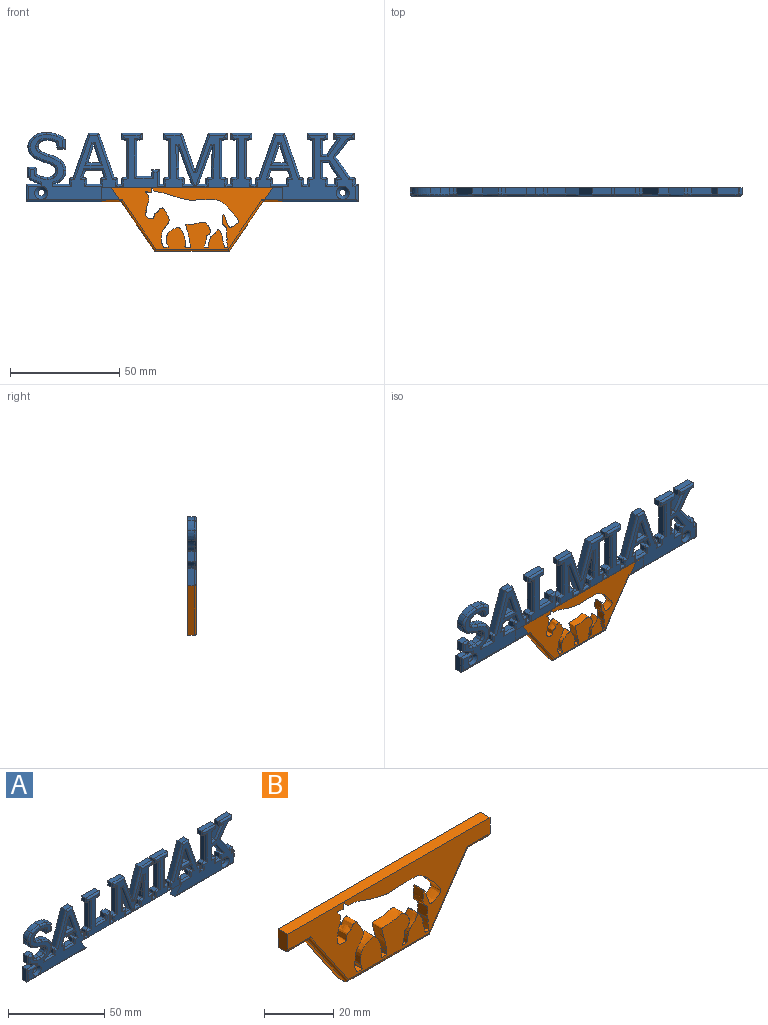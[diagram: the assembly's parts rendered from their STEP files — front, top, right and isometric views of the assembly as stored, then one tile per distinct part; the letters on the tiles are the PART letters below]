
ASSEMBLY  parts=2 mates=1
PART A: 335 faces, bbox 152.3x4.3x31.9 mm
  f0: plane 150x29.63mm, normal (0,-1,0), area 1480.1mm2, adj f3,f166,f167,f168,f169,f170,f171,f172
  f1: plane 152x31.63mm, normal (0,1,0), area 2472.2mm2, adj f2,f4,f5,f6,f7,f8,f9,f10
  f2: plane 43.45x3mm, normal (0,0,-1), area 130.3mm2, adj f1,f3,f47,f331
  f3: cylinder r=1mm len=43.45mm, axis (-1,0,0), area 66.9mm2, adj f0,f2,f276,f331
  f4: extruded ~3x1.6mm, area 5mm2, adj f1,f35,f165,f270
  f5: plane 3x2.77mm, normal (-1,0,0), area 8.3mm2, adj f1,f17,f160,f190
  f6: plane 6.49x3mm, normal (1,0,0), area 19.5mm2, adj f1,f7,f159,f166
  f7: plane 3.57x3mm, normal (0,0,1), area 10.7mm2, adj f1,f6,f8,f168
  f8: plane 3x2.93mm, normal (-1,0,0.08), area 8.8mm2, adj f1,f7,f9,f170
  f9: plane 6.58x3mm, normal (0,0,1), area 19.7mm2, adj f1,f8,f10,f172
  f10: plane 16.42x3mm, normal (1,0,0), area 49.3mm2, adj f1,f9,f11,f174
  f11: plane 3x2.49mm, normal (0.19,0,-0.98), area 7.6mm2, adj f1,f10,f12,f176
  f12: plane 3x2.82mm, normal (1,0,0), area 8.5mm2, adj f1,f11,f13,f178
  f13: plane 9.65x3mm, normal (0,0,1), area 28.9mm2, adj f1,f12,f14,f180
  f14: plane 3x2.82mm, normal (-1,0,0), area 8.5mm2, adj f1,f13,f15,f182
  f15: plane 3x2.48mm, normal (-0.19,0,-0.98), area 7.6mm2, adj f1,f14,f16,f184
  f16: plane 16.72x3mm, normal (-1,0,0), area 50.2mm2, adj f1,f15,f17,f186
  f17: plane 3x2.48mm, normal (-0.19,0,0.98), area 7.6mm2, adj f1,f5,f16,f188
  f18: plane 3.5x3mm, normal (0,0,-1), area 10.5mm2, adj f1,f19,f46,f234
  f19: plane 4.77x3mm, normal (1,0,0), area 14.3mm2, adj f1,f18,f20,f236
  f20: extruded ~3.71x3mm, area 13mm2, adj f1,f19,f21,f238
  f21: extruded ~4.9x3mm, area 15mm2, adj f1,f20,f22,f240
  f22: extruded ~6.03x3mm, area 19.3mm2, adj f1,f21,f23,f242
  f23: extruded ~4.63x3mm, area 16.3mm2, adj f1,f22,f24,f244
  f24: extruded ~4.51x3mm, area 15.5mm2, adj f1,f23,f25,f246
  f25: extruded ~6.28x3mm, area 20.8mm2, adj f1,f24,f26,f248
  f26: extruded ~3.33x3mm, area 11.1mm2, adj f1,f25,f27,f250
  f27: extruded ~3x2.16mm, area 7.3mm2, adj f1,f26,f28,f252
  f28: extruded ~3x2.1mm, area 7.2mm2, adj f1,f27,f29,f254
  f29: extruded ~3x2.92mm, area 9.2mm2, adj f1,f28,f30,f256
  f30: extruded ~3x2.7mm, area 8.2mm2, adj f1,f29,f31,f258
  f31: extruded ~3x1.91mm, area 6.4mm2, adj f1,f30,f32,f260
  f32: plane 3.31x3mm, normal (0.99,0,0.15), area 10.1mm2, adj f1,f31,f33,f262
  f33: plane 3.62x3mm, normal (0,0,1), area 10.8mm2, adj f1,f32,f34,f264
  f34: plane 4.87x3mm, normal (-1,0,0), area 14.6mm2, adj f1,f33,f35,f266
  f35: extruded ~3.72x3mm, area 13.4mm2, adj f1,f4,f34,f268
  f36: extruded ~3x2.9mm, area 9.6mm2, adj f1,f37,f163,f212
  f37: extruded ~4.72x3mm, area 16.5mm2, adj f1,f36,f38,f214
  f38: extruded ~4.62x3mm, area 15.6mm2, adj f1,f37,f39,f216
  f39: extruded ~5.85x3mm, area 19.7mm2, adj f1,f38,f40,f218
  f40: extruded ~3.79x3mm, area 12.4mm2, adj f1,f39,f41,f220
  f41: extruded ~3x1.94mm, area 7mm2, adj f1,f40,f42,f222
  f42: extruded ~3x2.09mm, area 7.3mm2, adj f1,f41,f43,f224
  f43: extruded ~3x2.97mm, area 9.4mm2, adj f1,f42,f44,f226
  f44: extruded ~3x2.48mm, area 7.5mm2, adj f1,f43,f45,f228
  f45: extruded ~3x1.78mm, area 5.7mm2, adj f1,f44,f46,f230
  f46: plane 3.2x3mm, normal (-0.98,0,-0.19), area 9.8mm2, adj f1,f18,f45,f232
  f47: plane 8.03x3mm, normal (-1,0,0), area 24.1mm2, adj f1,f2,f164,f276
  f48: plane 43.45x3mm, normal (0,0,-1), area 130.3mm2, adj f1,f49,f278,f332
  f49: plane 8.03x3mm, normal (1,0,0), area 24.1mm2, adj f1,f48,f151,f280
  f50: plane 5.35x3mm, normal (0,0,1), area 16mm2, adj f1,f51,f67,f324
  f51: plane 8.21x3mm, normal (0.95,0,-0.3), area 25.9mm2, adj f1,f50,f52,f326
  f52: plane 3x0.09mm, normal (0,0,-1), area 0.3mm2, adj f1,f51,f67,f327
  f53: plane 3x1.66mm, normal (-0.14,0,0.99), area 5mm2, adj f1,f54,f66,f204
  f54: plane 3x2.77mm, normal (-1,0,0), area 8.3mm2, adj f1,f53,f162,f206
  f55: plane 3x2.77mm, normal (1,0,0), area 8.3mm2, adj f1,f56,f161,f317
  f56: plane 3x1.61mm, normal (0.18,0,0.98), area 4.9mm2, adj f1,f55,f57,f315
  f57: plane 3.2x3mm, normal (0.95,0,-0.3), area 10.1mm2, adj f1,f56,f58,f313
  f58: plane 7.55x3mm, normal (0,0,-1), area 22.7mm2, adj f1,f57,f59,f312
  f59: plane 3.2x3mm, normal (-0.95,0,-0.3), area 10.1mm2, adj f1,f58,f60,f314
  f60: plane 3x1.62mm, normal (-0.17,0,0.98), area 4.9mm2, adj f1,f59,f61,f316
  f61: plane 3x2.77mm, normal (-1,0,0), area 8.3mm2, adj f1,f60,f161,f318
  f62: plane 3x2.77mm, normal (1,0,0), area 8.3mm2, adj f1,f63,f160,f194
  f63: plane 3x1.66mm, normal (0.14,0,0.99), area 5mm2, adj f1,f62,f64,f196
  f64: plane 20.26x7.04mm, normal (0.94,0,0.33), area 64.3mm2, adj f1,f63,f65,f198
  f65: plane 4.78x3mm, normal (0,0,1), area 14.4mm2, adj f1,f64,f66,f200
  f66: plane 20.26x7.09mm, normal (-0.94,0,0.33), area 64.4mm2, adj f1,f53,f65,f202
  f67: plane 8.21x3mm, normal (-0.95,0,-0.3), area 25.9mm2, adj f1,f50,f52,f325
  f68: plane 3x0.1mm, normal (-0.16,0,-0.99), area 0.3mm2, adj f1,f69,f94,f300
  f69: plane 10.29x3mm, normal (-1,0,0.04), area 30.9mm2, adj f1,f68,f70,f298
  f70: plane 3.66x3mm, normal (-1,0,0), area 11mm2, adj f1,f69,f71,f299
  f71: plane 3x2.48mm, normal (-0.19,0,0.98), area 7.6mm2, adj f1,f70,f72,f301
  f72: plane 3x2.77mm, normal (-1,0,0), area 8.3mm2, adj f1,f71,f157,f303
  f73: plane 3x2.77mm, normal (1,0,0), area 8.3mm2, adj f1,f74,f156,f197
  f74: plane 3x2.49mm, normal (0.19,0,0.98), area 7.6mm2, adj f1,f73,f75,f195
  f75: plane 16.72x3mm, normal (1,0,0), area 50.2mm2, adj f1,f74,f76,f193
  f76: plane 3x2.49mm, normal (0.19,0,-0.98), area 7.6mm2, adj f1,f75,f77,f191
  f77: plane 3x2.82mm, normal (1,0,0), area 8.5mm2, adj f1,f76,f78,f189
  f78: plane 8.61x3mm, normal (0,0,1), area 25.8mm2, adj f1,f77,f79,f187
  f79: plane 17.17x5.99mm, normal (-0.94,0,0.33), area 54.6mm2, adj f1,f78,f80,f185
  f80: plane 3x0.1mm, normal (0,0,1), area 0.3mm2, adj f1,f79,f81,f183
  f81: plane 17.17x5.94mm, normal (0.95,0,0.33), area 54.5mm2, adj f1,f80,f82,f181
  f82: plane 8.58x3mm, normal (0,0,1), area 25.7mm2, adj f1,f81,f83,f179
  f83: plane 3x2.82mm, normal (-1,0,0), area 8.5mm2, adj f1,f82,f84,f177
  f84: plane 3x2.48mm, normal (-0.19,0,-0.98), area 7.6mm2, adj f1,f83,f85,f175
  f85: plane 16.72x3mm, normal (-1,0,0), area 50.2mm2, adj f1,f84,f86,f173
  f86: plane 3x2.48mm, normal (-0.19,0,0.98), area 7.6mm2, adj f1,f85,f87,f171
  f87: plane 3x2.77mm, normal (-1,0,0), area 8.3mm2, adj f1,f86,f159,f169
  f88: plane 3x2.77mm, normal (1,0,0), area 8.3mm2, adj f1,f89,f158,f309
  f89: plane 3x2.49mm, normal (0.19,0,0.98), area 7.6mm2, adj f1,f88,f90,f307
  f90: plane 3.66x3mm, normal (1,0,0), area 11mm2, adj f1,f89,f91,f305
  f91: plane 10.23x3mm, normal (1,0,0.04), area 30.7mm2, adj f1,f90,f92,f306
  f92: plane 3x0.1mm, normal (0.16,0,-0.99), area 0.3mm2, adj f1,f91,f93,f308
  f93: plane 17.16x6.2mm, normal (-0.94,0,-0.34), area 54.7mm2, adj f1,f92,f158,f310
  f94: plane 17.23x6.23mm, normal (0.94,0,-0.34), area 55mm2, adj f1,f68,f157,f302
  f95: plane 3x2.82mm, normal (-1,0,0), area 8.5mm2, adj f1,f96,f105,f209
  f96: plane 3x2.49mm, normal (-0.19,0,-0.98), area 7.6mm2, adj f1,f95,f97,f207
  f97: plane 16.72x3mm, normal (-1,0,0), area 50.2mm2, adj f1,f96,f98,f205
  f98: plane 3x2.49mm, normal (-0.19,0,0.98), area 7.6mm2, adj f1,f97,f99,f203
  f99: plane 3x2.77mm, normal (-1,0,0), area 8.3mm2, adj f1,f98,f156,f201
  f100: plane 3x2.77mm, normal (1,0,0), area 8.3mm2, adj f1,f101,f155,f221
  f101: plane 3x2.49mm, normal (0.19,0,0.98), area 7.6mm2, adj f1,f100,f102,f219
  f102: plane 16.72x3mm, normal (1,0,0), area 50.2mm2, adj f1,f101,f103,f217
  f103: plane 3x2.49mm, normal (0.19,0,-0.98), area 7.6mm2, adj f1,f102,f104,f215
  f104: plane 3x2.82mm, normal (1,0,0), area 8.5mm2, adj f1,f103,f105,f213
  f105: plane 9.65x3mm, normal (0,0,1), area 28.9mm2, adj f1,f95,f104,f211
  f106: plane 5.35x3mm, normal (0,0,1), area 16mm2, adj f1,f107,f123,f320
  f107: plane 8.21x3mm, normal (0.95,0,-0.3), area 25.9mm2, adj f1,f106,f108,f322
  f108: plane 3x0.09mm, normal (0,0,-1), area 0.3mm2, adj f1,f107,f123,f323
  f109: plane 3x1.66mm, normal (-0.14,0,0.99), area 5mm2, adj f1,f110,f122,f227
  f110: plane 3x2.77mm, normal (-1,0,0), area 8.3mm2, adj f1,f109,f155,f225
  f111: plane 3x2.77mm, normal (1,0,0), area 8.3mm2, adj f1,f112,f154,f295
  f112: plane 3x1.61mm, normal (0.18,0,0.98), area 4.9mm2, adj f1,f111,f113,f293
  f113: plane 3.2x3mm, normal (0.95,0,-0.3), area 10.1mm2, adj f1,f112,f114,f291
  f114: plane 7.55x3mm, normal (0,0,-1), area 22.7mm2, adj f1,f113,f115,f290
  f115: plane 3.2x3mm, normal (-0.95,0,-0.3), area 10.1mm2, adj f1,f114,f116,f292
  f116: plane 3x1.62mm, normal (-0.17,0,0.98), area 4.9mm2, adj f1,f115,f117,f294
  f117: plane 3x2.77mm, normal (-1,0,0), area 8.3mm2, adj f1,f116,f154,f296
  f118: plane 3x2.77mm, normal (1,0,0), area 8.3mm2, adj f1,f119,f153,f237
  f119: plane 3x1.66mm, normal (0.14,0,0.99), area 5mm2, adj f1,f118,f120,f235
  f120: plane 20.26x7.04mm, normal (0.94,0,0.33), area 64.3mm2, adj f1,f119,f121,f233
  f121: plane 4.78x3mm, normal (0,0,1), area 14.4mm2, adj f1,f120,f122,f231
  f122: plane 20.26x7.09mm, normal (-0.94,0,0.33), area 64.4mm2, adj f1,f109,f121,f229
  f123: plane 8.21x3mm, normal (-0.95,0,-0.3), area 25.9mm2, adj f1,f106,f108,f321
  f124: plane 3x2.48mm, normal (-0.19,0,0.98), area 7.6mm2, adj f1,f125,f150,f243
  f125: plane 3x2.77mm, normal (-1,0,0), area 8.3mm2, adj f1,f124,f153,f241
  f126: plane 3x2.77mm, normal (1,0,0), area 8.3mm2, adj f1,f127,f152,f287
  f127: plane 3x2.37mm, normal (0.2,0,0.98), area 7.2mm2, adj f1,f126,f128,f285
  f128: plane 6.45x3mm, normal (1,0,0), area 19.3mm2, adj f1,f127,f129,f283
  f129: plane 3x2.61mm, normal (0,0,-1), area 7.8mm2, adj f1,f128,f130,f282
  f130: plane 6.74x4.48mm, normal (-0.83,0,-0.55), area 24.3mm2, adj f1,f129,f131,f284
  f131: plane 3x1.44mm, normal (-0.13,0,0.99), area 4.4mm2, adj f1,f130,f132,f286
  f132: plane 3x2.77mm, normal (-1,0,0), area 8.3mm2, adj f1,f131,f152,f288
  f133: plane 3x2.77mm, normal (1,0,0), area 8.3mm2, adj f1,f134,f151,f279
  f134: plane 3x2.34mm, normal (0.17,0,0.99), area 7.1mm2, adj f1,f133,f135,f277
  f135: plane 9.2x6.43mm, normal (0.82,0,0.57), area 33.7mm2, adj f1,f134,f136,f275
  f136: plane 7.65x5.73mm, normal (0.8,0,-0.6), area 28.7mm2, adj f1,f135,f137,f273
  f137: plane 3x2.53mm, normal (0.17,0,-0.99), area 7.7mm2, adj f1,f136,f138,f271
  f138: plane 3x2.82mm, normal (1,0,0), area 8.5mm2, adj f1,f137,f139,f269
  f139: plane 9.23x3mm, normal (0,0,1), area 27.7mm2, adj f1,f138,f140,f267
  f140: plane 3x2.82mm, normal (-1,0,0), area 8.5mm2, adj f1,f139,f141,f265
  f141: plane 3x1.38mm, normal (-0.14,0,-0.99), area 4.2mm2, adj f1,f140,f142,f263
  f142: plane 6.51x4.48mm, normal (-0.82,0,0.57), area 23.7mm2, adj f1,f141,f143,f261
  f143: plane 3x2.03mm, normal (0,0,1), area 6.1mm2, adj f1,f142,f144,f259
  f144: plane 6.22x3mm, normal (1,0,0), area 18.7mm2, adj f1,f143,f145,f257
  f145: plane 3x2.37mm, normal (0.2,0,-0.98), area 7.2mm2, adj f1,f144,f146,f255
  f146: plane 3x2.82mm, normal (1,0,0), area 8.5mm2, adj f1,f145,f147,f253
  f147: plane 9.52x3mm, normal (0,0,1), area 28.6mm2, adj f1,f146,f148,f251
  f148: plane 3x2.82mm, normal (-1,0,0), area 8.5mm2, adj f1,f147,f149,f249
  f149: plane 3x2.48mm, normal (-0.19,0,-0.98), area 7.6mm2, adj f1,f148,f150,f247
  f150: plane 16.72x3mm, normal (-1,0,0), area 50.2mm2, adj f1,f124,f149,f245
  f151: plane 3x1.31mm, normal (0,0,1), area 3.9mm2, adj f1,f49,f133,f281
  f152: plane 3.28x3mm, normal (0,0,1), area 9.8mm2, adj f1,f126,f132,f289
  f153: plane 3x1.54mm, normal (0,0,1), area 4.6mm2, adj f1,f118,f125,f239
  f154: plane 6.37x3mm, normal (0,0,1), area 19.1mm2, adj f1,f111,f117,f297
  f155: plane 3x1.54mm, normal (0,0,1), area 4.6mm2, adj f1,f100,f110,f223
  f156: plane 3x1.65mm, normal (0,0,1), area 4.9mm2, adj f1,f73,f99,f199
  f157: plane 3.4x3mm, normal (0,0,1), area 10.2mm2, adj f1,f72,f94,f304
  f158: plane 3.35x3mm, normal (0,0,1), area 10.1mm2, adj f1,f88,f93,f311
  f159: plane 3x1.68mm, normal (0,0,1), area 5mm2, adj f1,f6,f87,f167
  f160: plane 3x1.54mm, normal (0,0,1), area 4.6mm2, adj f1,f5,f62,f192
  f161: plane 6.37x3mm, normal (0,0,1), area 19.1mm2, adj f1,f55,f61,f319
  f162: plane 6.87x3mm, normal (0,0,1), area 20.6mm2, adj f1,f54,f163,f208
  f163: plane 3x0.02mm, normal (1,0,0), area 0.1mm2, adj f1,f36,f162,f210
  f164: plane 6.22x3mm, normal (0,0,1), area 18.7mm2, adj f1,f47,f165,f274
  f165: plane 3x0.01mm, normal (-1,0,0), area 0mm2, adj f1,f4,f164,f272
  f166: cylinder r=1mm len=7.49mm, axis (0,0,-1), area 10.2mm2, adj f0,f6,f167,f168
  f167: cylinder r=1mm len=3.68mm, axis (1,0,0), area 4.2mm2, adj f0,f159,f166,f169
  f168: cylinder r=1mm len=3.57mm, axis (1,0,0), area 4.1mm2, adj f0,f7,f166,f170
  f169: cylinder r=1mm len=3.77mm, axis (0,0,1), area 4.5mm2, adj f0,f87,f167,f171
  f170: cylinder r=1mm len=3.93mm, axis (0.08,0,1), area 4.6mm2, adj f0,f8,f168,f172
  f171: cylinder r=1mm len=3.48mm, axis (0.98,0,0.19), area 4mm2, adj f0,f86,f169,f173
  f172: cylinder r=1mm len=8.5mm, axis (1,0,0), area 11.8mm2, adj f0,f9,f170,f174
  f173: cylinder r=1mm len=18.37mm, axis (0,0,1), area 27.6mm2, adj f0,f85,f171,f175
  f174: cylinder r=1mm len=18.25mm, axis (0,0,-1), area 27.2mm2, adj f0,f10,f172,f176
  f175: cylinder r=1mm len=3.48mm, axis (-0.98,0,0.19), area 4mm2, adj f0,f84,f173,f177
  f176: cylinder r=1mm len=3.49mm, axis (-0.98,0,-0.19), area 4mm2, adj f0,f11,f174,f178
  f177: cylinder r=1mm len=2.82mm, axis (0,0,1), area 3mm2, adj f0,f83,f175,f179
  f178: cylinder r=1mm len=2.82mm, axis (0,0,-1), area 3mm2, adj f0,f12,f176,f180
  f179: cylinder r=1mm len=8.58mm, axis (1,0,0), area 12.1mm2, adj f0,f82,f177,f181
  f180: cylinder r=1mm len=9.65mm, axis (1,0,0), area 13.6mm2, adj f0,f13,f178,f182
  f181: cylinder r=1mm len=18.17mm, axis (0.33,0,-0.95), area 28.5mm2, adj f0,f81,f179,f183
  f182: cylinder r=1mm len=2.82mm, axis (0,0,1), area 3mm2, adj f0,f14,f180,f184
  f183: cylinder r=1mm len=1.52mm, axis (1,0,0), area 1mm2, adj f0,f80,f181,f185
  f184: cylinder r=1mm len=3.48mm, axis (-0.98,0,0.19), area 4mm2, adj f0,f15,f182,f186
  f185: cylinder r=1mm len=18.17mm, axis (0.33,0,0.94), area 28.6mm2, adj f0,f79,f183,f187
  f186: cylinder r=1mm len=18.37mm, axis (0,0,1), area 27.6mm2, adj f0,f16,f184,f188
  f187: cylinder r=1mm len=8.61mm, axis (1,0,0), area 12.2mm2, adj f0,f78,f185,f189
  f188: cylinder r=1mm len=3.48mm, axis (0.98,0,0.19), area 4mm2, adj f0,f17,f186,f190
  f189: cylinder r=1mm len=2.82mm, axis (0,0,-1), area 3mm2, adj f0,f77,f187,f191
  f190: cylinder r=1mm len=3.77mm, axis (0,0,1), area 4.5mm2, adj f0,f5,f188,f192
  f191: cylinder r=1mm len=3.49mm, axis (-0.98,0,-0.19), area 4mm2, adj f0,f76,f189,f193
  f192: cylinder r=1mm len=3.54mm, axis (1,0,0), area 4mm2, adj f0,f160,f190,f194
  f193: cylinder r=1mm len=18.37mm, axis (0,0,-1), area 27.6mm2, adj f0,f75,f191,f195
  f194: cylinder r=1mm len=3.77mm, axis (0,0,-1), area 4.5mm2, adj f0,f62,f192,f196
  f195: cylinder r=1mm len=3.49mm, axis (0.98,0,-0.19), area 4mm2, adj f0,f74,f193,f197
  f196: cylinder r=1mm len=2.41mm, axis (0.99,0,-0.14), area 2.4mm2, adj f0,f63,f194,f198
  f197: cylinder r=1mm len=3.77mm, axis (0,0,-1), area 4.5mm2, adj f0,f73,f195,f199
  f198: cylinder r=1mm len=21.16mm, axis (0.33,0,-0.94), area 33.6mm2, adj f0,f64,f196,f200
  f199: cylinder r=1mm len=3.65mm, axis (1,0,0), area 4.2mm2, adj f0,f156,f197,f201
  f200: cylinder r=1mm len=4.78mm, axis (1,0,0), area 6.4mm2, adj f0,f65,f198,f202
  f201: cylinder r=1mm len=3.77mm, axis (0,0,1), area 4.5mm2, adj f0,f99,f199,f203
  f202: cylinder r=1mm len=21.16mm, axis (0.33,0,0.94), area 33.6mm2, adj f0,f66,f200,f204
  f203: cylinder r=1mm len=3.49mm, axis (0.98,0,0.19), area 4mm2, adj f0,f98,f201,f205
  f204: cylinder r=1mm len=2.41mm, axis (0.99,0,0.14), area 2.4mm2, adj f0,f53,f202,f206
  f205: cylinder r=1mm len=18.37mm, axis (0,0,1), area 27.6mm2, adj f0,f97,f203,f207
  f206: cylinder r=1mm len=3.77mm, axis (0,0,1), area 4.5mm2, adj f0,f54,f204,f208
  f207: cylinder r=1mm len=3.49mm, axis (-0.98,0,0.19), area 4mm2, adj f0,f96,f205,f209
  f208: cylinder r=1mm len=8.87mm, axis (1,0,0), area 12.4mm2, adj f0,f162,f206,f210
  f209: cylinder r=1mm len=2.82mm, axis (0,0,1), area 3mm2, adj f0,f95,f207,f211
  f210: cylinder r=1mm len=1.83mm, axis (0,0,1), area 1.1mm2, adj f0,f163,f208,f212
  f211: cylinder r=1mm len=9.65mm, axis (1,0,0), area 13.6mm2, adj f0,f105,f209,f213
  f212: bspline ~5.54x3.25mm, area 5.5mm2, adj f0,f36,f210,f214
  f213: cylinder r=1mm len=2.82mm, axis (0,0,-1), area 3mm2, adj f0,f104,f211,f215
  f214: bspline ~5.93x4.09mm, area 8.1mm2, adj f0,f37,f212,f216
  f215: cylinder r=1mm len=3.49mm, axis (-0.98,0,-0.19), area 4mm2, adj f0,f103,f213,f217
  f216: bspline ~7.17x3.8mm, area 7.7mm2, adj f0,f38,f214,f218
  f217: cylinder r=1mm len=18.37mm, axis (0,0,-1), area 27.6mm2, adj f0,f102,f215,f219
  f218: bspline ~8.49x4.64mm, area 10mm2, adj f0,f39,f216,f220
  f219: cylinder r=1mm len=3.49mm, axis (0.98,0,-0.19), area 4mm2, adj f0,f101,f217,f221
  f220: bspline ~5.52x2.97mm, area 6.7mm2, adj f0,f40,f218,f222
  f221: cylinder r=1mm len=3.77mm, axis (0,0,-1), area 4.5mm2, adj f0,f100,f219,f223
  f222: bspline ~3.7x2.58mm, area 4.2mm2, adj f0,f41,f220,f224
  f223: cylinder r=1mm len=3.54mm, axis (1,0,0), area 4mm2, adj f0,f155,f221,f225
  f224: bspline ~3.89x2.54mm, area 4.3mm2, adj f0,f42,f222,f226
  f225: cylinder r=1mm len=3.77mm, axis (0,0,1), area 4.5mm2, adj f0,f110,f223,f227
  f226: bspline ~4.93x1.89mm, area 5.3mm2, adj f0,f43,f224,f228
  f227: cylinder r=1mm len=2.41mm, axis (0.99,0,0.14), area 2.4mm2, adj f0,f109,f225,f229
  f228: bspline ~3.3x1.4mm, area 4.1mm2, adj f0,f44,f226,f230
  f229: cylinder r=1mm len=21.16mm, axis (0.33,0,0.94), area 33.6mm2, adj f0,f122,f227,f231
  f230: bspline ~3.75x2.33mm, area 3.5mm2, adj f0,f45,f228,f232
  f231: cylinder r=1mm len=4.78mm, axis (1,0,0), area 6.4mm2, adj f0,f121,f229,f233
  f232: cylinder r=1mm len=3.82mm, axis (-0.19,0,0.98), area 4.8mm2, adj f0,f46,f230,f234
  f233: cylinder r=1mm len=21.16mm, axis (0.33,0,-0.94), area 33.6mm2, adj f0,f120,f231,f235
  f234: cylinder r=1mm len=3.5mm, axis (-1,0,0), area 4.1mm2, adj f0,f18,f232,f236
  f235: cylinder r=1mm len=2.41mm, axis (0.99,0,-0.14), area 2.4mm2, adj f0,f119,f233,f237
  f236: cylinder r=1mm len=4.77mm, axis (0,0,-1), area 6.3mm2, adj f0,f19,f234,f238
  f237: cylinder r=1mm len=3.77mm, axis (0,0,-1), area 4.5mm2, adj f0,f118,f235,f239
  f238: bspline ~5.31x3.52mm, area 6.2mm2, adj f0,f20,f236,f240
  f239: cylinder r=1mm len=3.54mm, axis (1,0,0), area 4mm2, adj f0,f153,f237,f241
  f240: bspline ~6.2x2.17mm, area 7.6mm2, adj f0,f21,f238,f242
  f241: cylinder r=1mm len=3.77mm, axis (0,0,1), area 4.5mm2, adj f0,f125,f239,f243
  f242: bspline ~7.58x3.65mm, area 9.7mm2, adj f0,f22,f240,f244
  f243: cylinder r=1mm len=3.48mm, axis (0.98,0,0.19), area 4mm2, adj f0,f124,f241,f245
  f244: bspline ~6.88x4.13mm, area 8mm2, adj f0,f23,f242,f246
  f245: cylinder r=1mm len=18.37mm, axis (0,0,1), area 27.6mm2, adj f0,f150,f243,f247
  f246: bspline ~6.71x3.82mm, area 7.6mm2, adj f0,f24,f244,f248
  f247: cylinder r=1mm len=3.48mm, axis (-0.98,0,0.19), area 4mm2, adj f0,f149,f245,f249
  f248: bspline ~9.03x4.73mm, area 10.7mm2, adj f0,f25,f246,f250
  f249: cylinder r=1mm len=2.82mm, axis (0,0,1), area 3mm2, adj f0,f148,f247,f251
  f250: bspline ~5.31x3.13mm, area 6mm2, adj f0,f26,f248,f252
  f251: cylinder r=1mm len=9.52mm, axis (1,0,0), area 13.4mm2, adj f0,f147,f249,f253
  f252: bspline ~3.94x2.42mm, area 4.3mm2, adj f0,f27,f250,f254
  f253: cylinder r=1mm len=2.82mm, axis (0,0,-1), area 3mm2, adj f0,f146,f251,f255
  f254: bspline ~3.89x2.49mm, area 4.3mm2, adj f0,f28,f252,f256
  f255: cylinder r=1mm len=3.37mm, axis (-0.98,0,-0.2), area 3.8mm2, adj f0,f145,f253,f257
  f256: bspline ~5.2x2.15mm, area 5.2mm2, adj f0,f29,f254,f258
  f257: cylinder r=1mm len=8.04mm, axis (0,0,-1), area 11.2mm2, adj f0,f144,f255,f259
  f258: bspline ~4.08x1.54mm, area 4.5mm2, adj f0,f30,f256,f260
  f259: cylinder r=1mm len=3.56mm, axis (1,0,0), area 4.4mm2, adj f0,f143,f257,f261
  f260: bspline ~3.87x2.69mm, area 3.9mm2, adj f0,f31,f258,f262
  f261: cylinder r=1mm len=8.85mm, axis (0.57,0,0.82), area 14.1mm2, adj f0,f142,f259,f263
  f262: cylinder r=1mm len=3.84mm, axis (0.15,0,-0.99), area 4.9mm2, adj f0,f32,f260,f264
  f263: cylinder r=1mm len=3.12mm, axis (-0.99,0,0.14), area 2.8mm2, adj f0,f141,f261,f265
  f264: cylinder r=1mm len=3.62mm, axis (1,0,0), area 4.2mm2, adj f0,f33,f262,f266
  f265: cylinder r=1mm len=2.82mm, axis (0,0,1), area 3mm2, adj f0,f140,f263,f267
  f266: cylinder r=1mm len=4.87mm, axis (0,0,1), area 6.5mm2, adj f0,f34,f264,f268
  f267: cylinder r=1mm len=9.23mm, axis (1,0,0), area 12.9mm2, adj f0,f139,f265,f269
  f268: bspline ~4.54x3.47mm, area 6.5mm2, adj f0,f35,f266,f270
  f269: cylinder r=1mm len=2.82mm, axis (0,0,-1), area 3mm2, adj f0,f138,f267,f271
  f270: bspline ~4.41x2.16mm, area 3.2mm2, adj f0,f4,f268,f272
  f271: cylinder r=1mm len=3.09mm, axis (-0.99,0,-0.17), area 3.7mm2, adj f0,f137,f269,f273
  f272: cylinder r=1mm len=1.83mm, axis (0,0,-1), area 1.1mm2, adj f0,f165,f270,f274
  f273: cylinder r=1mm len=9.15mm, axis (-0.6,0,-0.8), area 15.9mm2, adj f0,f136,f271,f275
  f274: cylinder r=1mm len=7.22mm, axis (1,0,0), area 9.8mm2, adj f0,f164,f272,f276
  f275: cylinder r=1mm len=10.71mm, axis (0.57,0,-0.82), area 18.5mm2, adj f0,f135,f273,f277
  f276: cylinder r=1mm len=8.03mm, axis (0,0,1), area 11mm2, adj f0,f3,f47,f274
  f277: cylinder r=1mm len=2.92mm, axis (0.99,0,-0.17), area 3.4mm2, adj f0,f134,f275,f279
  f278: cylinder r=1mm len=43.45mm, axis (-1,0,0), area 66.9mm2, adj f0,f48,f280,f332
  f279: cylinder r=1mm len=3.77mm, axis (0,0,-1), area 4.5mm2, adj f0,f133,f277,f281
  f280: cylinder r=1mm len=8.03mm, axis (0,0,-1), area 11mm2, adj f0,f49,f278,f281
  f281: cylinder r=1mm len=2.31mm, axis (1,0,0), area 2.1mm2, adj f0,f151,f279,f280
  f282: cylinder r=1mm len=4.14mm, axis (-1,0,0), area 5.3mm2, adj f0,f129,f283,f284
  f283: cylinder r=1mm len=8.27mm, axis (0,0,-1), area 11.6mm2, adj f0,f128,f282,f285
  f284: cylinder r=1mm len=9.08mm, axis (-0.55,0,0.83), area 14.4mm2, adj f0,f130,f282,f286
  f285: cylinder r=1mm len=3.37mm, axis (0.98,0,-0.2), area 3.8mm2, adj f0,f127,f283,f287
  f286: cylinder r=1mm len=3.16mm, axis (0.99,0,0.13), area 2.9mm2, adj f0,f131,f284,f288
  f287: cylinder r=1mm len=3.77mm, axis (0,0,-1), area 4.5mm2, adj f0,f126,f285,f289
  f288: cylinder r=1mm len=3.77mm, axis (0,0,1), area 4.5mm2, adj f0,f132,f286,f289
  f289: cylinder r=1mm len=5.28mm, axis (1,0,0), area 6.7mm2, adj f0,f152,f287,f288
  f290: cylinder r=1mm len=9.01mm, axis (-1,0,0), area 13mm2, adj f0,f114,f291,f292
  f291: cylinder r=1mm len=5.29mm, axis (-0.3,0,-0.95), area 6.8mm2, adj f0,f113,f290,f293
  f292: cylinder r=1mm len=5.29mm, axis (-0.3,0,0.95), area 6.8mm2, adj f0,f115,f290,f294
  f293: cylinder r=1mm len=2.91mm, axis (0.98,0,-0.18), area 2.8mm2, adj f0,f112,f291,f295
  f294: cylinder r=1mm len=2.92mm, axis (0.98,0,0.17), area 2.8mm2, adj f0,f116,f292,f296
  f295: cylinder r=1mm len=3.77mm, axis (0,0,-1), area 4.5mm2, adj f0,f111,f293,f297
  f296: cylinder r=1mm len=3.77mm, axis (0,0,1), area 4.5mm2, adj f0,f117,f294,f297
  f297: cylinder r=1mm len=8.37mm, axis (1,0,0), area 11.6mm2, adj f0,f154,f295,f296
  f298: cylinder r=1mm len=11.23mm, axis (0.04,0,1), area 16.9mm2, adj f0,f69,f299,f300
  f299: cylinder r=1mm len=4.49mm, axis (0,0,1), area 6.4mm2, adj f0,f70,f298,f301
  f300: cylinder r=1mm len=1.95mm, axis (-0.99,0,0.16), area 1.1mm2, adj f0,f68,f298,f302
  f301: cylinder r=1mm len=3.48mm, axis (0.98,0,0.19), area 4mm2, adj f0,f71,f299,f303
  f302: cylinder r=1mm len=19.68mm, axis (-0.34,0,-0.94), area 30.5mm2, adj f0,f94,f300,f304
  f303: cylinder r=1mm len=3.77mm, axis (0,0,1), area 4.5mm2, adj f0,f72,f301,f304
  f304: cylinder r=1mm len=5.83mm, axis (1,0,0), area 7.2mm2, adj f0,f157,f302,f303
  f305: cylinder r=1mm len=4.49mm, axis (0,0,-1), area 6.4mm2, adj f0,f90,f306,f307
  f306: cylinder r=1mm len=11.16mm, axis (0.04,0,-1), area 16.8mm2, adj f0,f91,f305,f308
  f307: cylinder r=1mm len=3.49mm, axis (0.98,0,-0.19), area 4mm2, adj f0,f89,f305,f309
  f308: cylinder r=1mm len=1.95mm, axis (-0.99,0,-0.16), area 1.1mm2, adj f0,f92,f306,f310
  f309: cylinder r=1mm len=3.77mm, axis (0,0,-1), area 4.5mm2, adj f0,f88,f307,f311
  f310: cylinder r=1mm len=19.62mm, axis (-0.34,0,0.94), area 30.4mm2, adj f0,f93,f308,f311
  f311: cylinder r=1mm len=5.78mm, axis (1,0,0), area 7.2mm2, adj f0,f158,f309,f310
  f312: cylinder r=1mm len=9.01mm, axis (-1,0,0), area 13mm2, adj f0,f58,f313,f314
  f313: cylinder r=1mm len=5.29mm, axis (-0.3,0,-0.95), area 6.8mm2, adj f0,f57,f312,f315
  f314: cylinder r=1mm len=5.29mm, axis (-0.3,0,0.95), area 6.8mm2, adj f0,f59,f312,f316
  f315: cylinder r=1mm len=2.91mm, axis (0.98,0,-0.18), area 2.8mm2, adj f0,f56,f313,f317
  f316: cylinder r=1mm len=2.92mm, axis (0.98,0,0.17), area 2.8mm2, adj f0,f60,f314,f318
  f317: cylinder r=1mm len=3.77mm, axis (0,0,-1), area 4.5mm2, adj f0,f55,f315,f319
  f318: cylinder r=1mm len=3.77mm, axis (0,0,1), area 4.5mm2, adj f0,f61,f316,f319
  f319: cylinder r=1mm len=8.37mm, axis (1,0,0), area 11.6mm2, adj f0,f161,f317,f318
  f320: cylinder r=1mm len=8.09mm, axis (1,0,0), area 10.6mm2, adj f0,f106,f321,f322
  f321: cylinder r=1mm len=10.51mm, axis (-0.3,0,0.95), area 15.2mm2, adj f0,f123,f320,f323
  f322: cylinder r=1mm len=10.51mm, axis (-0.3,0,-0.95), area 15.2mm2, adj f0,f107,f320,f323
  f323: cylinder r=1mm len=1.55mm, axis (-1,0,0), area 1mm2, adj f0,f108,f321,f322
  f324: cylinder r=1mm len=8.09mm, axis (1,0,0), area 10.6mm2, adj f0,f50,f325,f326
  f325: cylinder r=1mm len=10.51mm, axis (-0.3,0,0.95), area 15.2mm2, adj f0,f67,f324,f327
  f326: cylinder r=1mm len=10.51mm, axis (-0.3,0,-0.95), area 15.2mm2, adj f0,f51,f324,f327
  f327: cylinder r=1mm len=1.55mm, axis (-1,0,0), area 1mm2, adj f0,f52,f325,f326
  f328: cylinder r=1.5mm len=3mm, axis (0,-1,0), area 23.6mm2, adj f1,f333
  f329: cylinder r=1.5mm len=3mm, axis (0,-1,0), area 23.6mm2, adj f1,f334
  f330: plane 74x4mm, normal (0,0,-1), area 296mm2, adj f0,f1,f331,f332
  f331: plane 6.81x4.73mm, normal (0.83,0,0.56), area 31.3mm2, adj f0,f1,f2,f3,f330
  f332: plane 6.81x4.73mm, normal (-0.83,0,0.56), area 31.3mm2, adj f0,f1,f48,f278,f330
  f333: cone r=3mm half-angle=45deg, axis (0,-1,0), area 30mm2, adj f0,f328
  f334: cone r=1.5mm half-angle=45deg, axis (0,-1,0), area 30mm2, adj f0,f329
PART B: 45 faces, bbox 82.6x4x29.4 mm
  f0: plane 22.83x15.55mm, normal (0.83,0,-0.56), area 82.9mm2, adj f2,f3,f38,f43
  f1: plane 82.6x28.36mm, normal (0,-1,0), area 1035mm2, adj f4,f5,f6,f7,f8,f9,f10,f11
  f2: plane 34x3mm, normal (0,0,-1), area 102mm2, adj f0,f3,f35,f42
  f3: plane 82.6x29.36mm, normal (0,1,0), area 1141.7mm2, adj f0,f2,f4,f5,f6,f7,f8,f9
  f4: extruded ~17.98x10.7mm, area 134.8mm2, adj f1,f3,f22,f34
  f5: extruded ~4x0.82mm, area 3.6mm2, adj f1,f3,f33,f34
  f6: extruded ~4x3.36mm, area 14.7mm2, adj f1,f3,f26,f31
  f7: extruded ~4.4x4mm, area 17.9mm2, adj f1,f3,f11,f30
  f8: extruded ~4x2.47mm, area 10.1mm2, adj f1,f3,f9,f29
  f9: extruded ~5.62x4.23mm, area 29.3mm2, adj f1,f3,f8,f31
  f10: extruded ~11.21x9.52mm, area 111.7mm2, adj f1,f3,f19,f28
  f11: extruded ~11.81x7.31mm, area 113.7mm2, adj f1,f3,f7,f20
  f12: extruded ~4x0.6mm, area 2.7mm2, adj f1,f3,f13,f24
  f13: plane 4x2.11mm, normal (0,0,1), area 8.4mm2, adj f1,f3,f12,f14
  f14: extruded ~4x1.76mm, area 7.5mm2, adj f1,f3,f13,f15
  f15: extruded ~8.67x7.27mm, area 74mm2, adj f1,f3,f14,f16
  f16: extruded ~4x1.84mm, area 7.6mm2, adj f1,f3,f15,f25
  f17: extruded ~4x0.93mm, area 3.8mm2, adj f1,f3,f18,f25
  f18: extruded ~4x0.1mm, area 0.4mm2, adj f1,f3,f17,f19
  f19: extruded ~4x1.07mm, area 4.3mm2, adj f1,f3,f10,f18
  f20: extruded ~36.29x10.72mm, area 159mm2, adj f1,f3,f11,f21
  f21: extruded ~4x1.96mm, area 9.3mm2, adj f1,f3,f20,f33
  f22: extruded ~4x0.45mm, area 1.8mm2, adj f1,f3,f4,f23
  f23: extruded ~4x2.37mm, area 9.8mm2, adj f1,f3,f22,f24
  f24: extruded ~4x1.21mm, area 5.4mm2, adj f1,f3,f12,f23
  f25: plane 4x2.38mm, normal (0,0,1), area 9.5mm2, adj f1,f3,f16,f17
  f26: plane 4x0.02mm, normal (0.17,0,-0.99), area 0.1mm2, adj f1,f3,f6,f27
  f27: extruded ~4.3x4mm, area 17.7mm2, adj f1,f3,f26,f30
  f28: extruded ~4x1.91mm, area 8mm2, adj f1,f3,f10,f29
  f29: plane 4x1.87mm, normal (0,0,1), area 7.5mm2, adj f1,f3,f8,f28
  f30: plane 4x1.64mm, normal (0,0,1), area 6.6mm2, adj f1,f3,f7,f27
  f31: extruded ~4x0.53mm, area 2.6mm2, adj f1,f3,f6,f9
  f32: plane 82.6x4mm, normal (0,0,1), area 330.4mm2, adj f1,f3,f37,f39
  f33: extruded ~4x1.39mm, area 5.6mm2, adj f1,f3,f5,f21
  f34: extruded ~4x2.5mm, area 11.8mm2, adj f1,f3,f4,f5
  f35: plane 22.83x15.55mm, normal (-0.83,0,-0.56), area 82.9mm2, adj f2,f3,f36,f41
  f36: plane 8.75x3mm, normal (0,0,-1), area 26.2mm2, adj f3,f35,f37,f40
  f37: plane 6.53x4mm, normal (-1,0,0), area 25.9mm2, adj f1,f3,f32,f36,f40
  f38: plane 8.75x3mm, normal (0,0,-1), area 26.2mm2, adj f0,f3,f39,f44
  f39: plane 6.53x4mm, normal (1,0,0), area 25.9mm2, adj f1,f3,f32,f38,f44
  f40: cylinder r=1mm len=9.28mm, axis (1,0,0), area 14mm2, adj f1,f36,f37,f41
  f41: cylinder r=1mm len=23.83mm, axis (0.56,0,-0.83), area 43.4mm2, adj f1,f35,f40,f42
  f42: cylinder r=1mm len=34mm, axis (-1,0,0), area 52.8mm2, adj f1,f2,f41,f43
  f43: cylinder r=1mm len=23.83mm, axis (0.56,0,0.83), area 43.4mm2, adj f0,f1,f42,f44
  f44: cylinder r=1mm len=9.28mm, axis (1,0,0), area 14mm2, adj f1,f38,f39,f43
PLACE A t=(-15.98,1.59,5.21)mm
PLACE B t=(-15.98,1.59,-8.35)mm
MATE fastened B.f32 <-> A.f330  axis (0,0,1) through (-15.98,-0.41,3.74)mm
